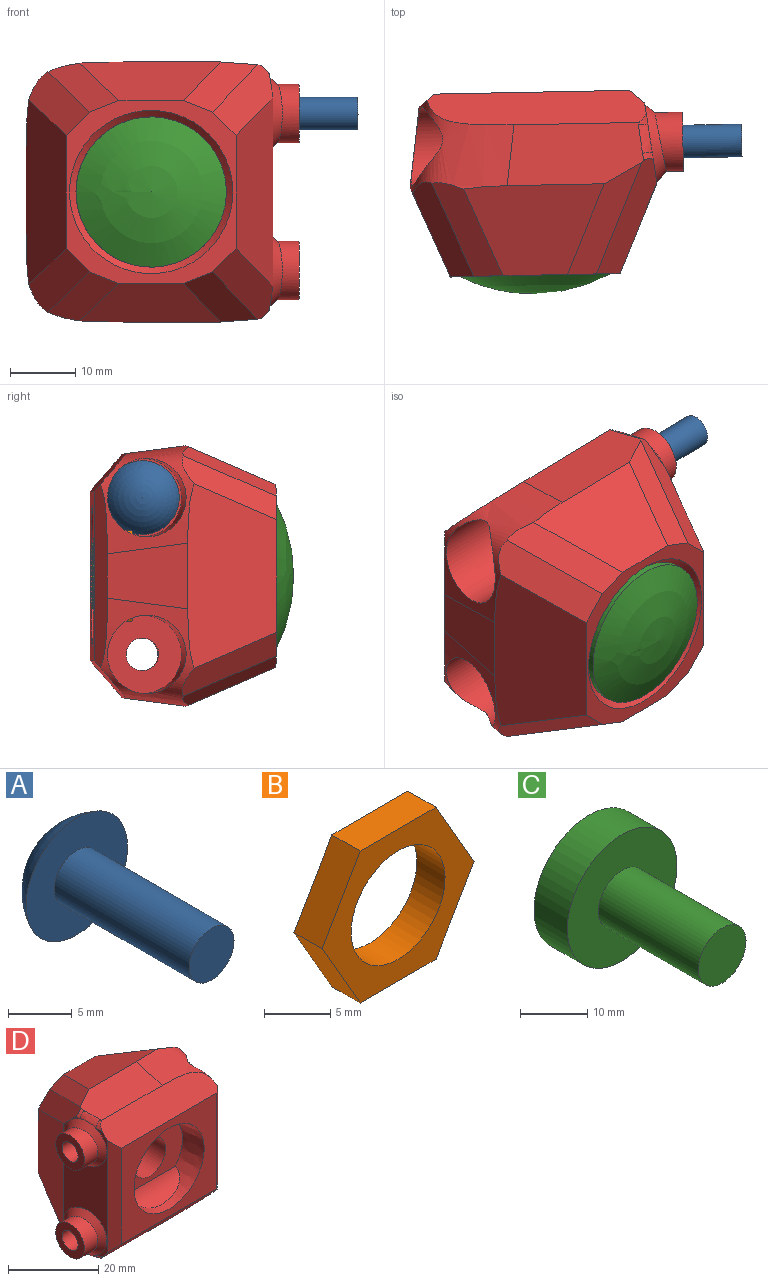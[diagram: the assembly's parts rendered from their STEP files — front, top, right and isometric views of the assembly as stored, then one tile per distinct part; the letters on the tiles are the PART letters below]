
ASSEMBLY  parts=4 mates=4
PART A: 4 faces, bbox 11.3x18.5x11.3 mm
  f0: plane 11.3x11.3mm, normal (0,-1,0), area 80.7mm2, adj f1,f3
  f1: cylinder r=2.5mm len=15mm, axis (0,-1,0), area 235.6mm2, adj f0,f2
  f2: plane 5x5mm, normal (0,-1,0), area 19.6mm2, adj f1
  f3: sphere r=6.31mm, area 138.8mm2, adj f0
PART B: 9 faces, bbox 16.2x3x14 mm
  f0: plane 7x4.04mm, normal (0.87,0,-0.5), area 24.2mm2, adj f1,f5,f7,f8
  f1: plane 7x4.04mm, normal (0.87,0,0.5), area 24.2mm2, adj f0,f2,f7,f8
  f2: plane 8.08x3mm, normal (0,0,1), area 24.2mm2, adj f1,f3,f7,f8
  f3: plane 7x4.04mm, normal (-0.87,0,0.5), area 24.2mm2, adj f2,f4,f7,f8
  f4: plane 7x4.04mm, normal (-0.87,0,-0.5), area 24.2mm2, adj f3,f5,f7,f8
  f5: plane 8.08x3mm, normal (0,0,-1), area 24.2mm2, adj f0,f4,f7,f8
  f6: cylinder r=5mm len=10mm, axis (0,1,0), area 94.2mm2, adj f7,f8
  f7: plane 16.17x14mm, normal (0,-1,0), area 91.2mm2, adj f0,f1,f2,f3,f4,f5,f6
  f8: plane 16.17x14mm, normal (0,1,0), area 91.2mm2, adj f0,f1,f2,f3,f4,f5,f6
PART C: 5 faces, bbox 23x30.8x23 mm
  f0: plane 10x10mm, normal (0,-1,0), area 78.5mm2, adj f4
  f1: sphere r=24.85mm, area 440.5mm2, adj f2
  f2: cylinder r=11.5mm len=23mm, axis (0,-1,0), area 505.8mm2, adj f1,f3
  f3: plane 23x23mm, normal (0,-1,0), area 336.9mm2, adj f2,f4
  f4: cylinder r=5mm len=21mm, axis (0,-1,0), area 659.7mm2, adj f0,f3
PART D: 48 faces, bbox 46.2x32.5x44.3 mm
  f0: cylinder r=5mm len=15mm, axis (0,-1,0), area 471.2mm2, adj f4,f15
  f1: plane 30x26mm, normal (0,-1,0), area 399.9mm2, adj f16,f26,f27,f28,f29
  f2: plane 28x26mm, normal (0,1,0), area 169.9mm2, adj f21,f22,f23,f24,f25,f30,f31,f32
  f3: cylinder r=11.5mm len=23mm, axis (0,1,0), area 433.5mm2, adj f4,f25
  f4: plane 23x23mm, normal (0,1,0), area 336.9mm2, adj f0,f3
  f5: cylinder r=2.5mm len=6mm, axis (1,0,0), area 94.2mm2, adj f6,f14
  f6: plane 12x12mm, normal (1,0,0), area 93.5mm2, adj f5,f7
  f7: cylinder r=6mm len=33.8mm, axis (1,0,0), area 1145.8mm2, adj f6,f15,f16,f47
  f8: cylinder r=2.5mm len=6mm, axis (1,0,0), area 94.2mm2, adj f9,f12
  f9: plane 12x12mm, normal (1,0,0), area 93.5mm2, adj f8,f10
  f10: cylinder r=6mm len=35.06mm, axis (1,0,0), area 1222.3mm2, adj f9,f15,f16,f46
  f11: cylinder r=4.5mm len=9mm, axis (1,0,0), area 108.4mm2, adj f12,f39
  f12: plane 9x9mm, normal (-1,0,0), area 44mm2, adj f8,f11
  f13: cylinder r=4.5mm len=9mm, axis (1,0,0), area 96.4mm2, adj f14,f38
  f14: plane 9x9mm, normal (-1,0,0), area 44mm2, adj f5,f13
  f15: plane 20.4x12.69mm, normal (0,-1,0), area 162.4mm2, adj f0,f7,f10,f16
  f16: cone r=9mm half-angle=7.6deg, axis (0,-1,0), area 286.3mm2, adj f1,f7,f10,f15
  f17: plane 21.17x9.47mm, normal (0,-0.13,-0.99), area 178.3mm2, adj f23,f28,f30,f34,f43,f44,f45,f47
  f18: plane 12.26x10.06mm, normal (0.99,-0.13,0), area 104.2mm2, adj f24,f27,f46,f47
  f19: plane 35.91x12.27mm, normal (-0.99,-0.13,0), area 194.7mm2, adj f21,f26,f28,f29,f30,f32,f38,f39
  f20: plane 21.17x9.47mm, normal (0,-0.13,0.99), area 178.2mm2, adj f22,f29,f32,f36,f40,f41,f42,f46
  f21: plane 29.05x13.76mm, normal (-0.92,0.39,0), area 346.6mm2, adj f2,f19,f30,f32
  f22: plane 22x14.26mm, normal (0,0.39,0.92), area 235.3mm2, adj f2,f20,f36,f37,f46
  f23: plane 22x14.26mm, normal (0,0.39,-0.92), area 235.3mm2, adj f2,f17,f34,f35,f47
  f24: plane 30.68x16.23mm, normal (0.92,0.39,0), area 341.1mm2, adj f2,f18,f31,f33,f46,f47
  f25: cone r=11.5mm half-angle=45deg, axis (0,1,0), area 106.6mm2, adj f2,f3
  f26: plane 30.53x2.26mm, normal (-0.66,-0.75,0), area 85.1mm2, adj f1,f19,f28,f29
  f27: plane 32.1x6.26mm, normal (0.66,-0.75,0), area 75.3mm2, adj f1,f18,f28,f29,f46,f47
  f28: plane 33.54x5.66mm, normal (0,-0.75,-0.66), area 234.6mm2, adj f1,f17,f19,f26,f27,f43,f47
  f29: plane 33.54x5.66mm, normal (0,-0.75,0.66), area 234.6mm2, adj f1,f19,f20,f26,f27,f40,f46
  f30: plane 18.01x11.38mm, normal (-0.6,0.52,-0.6), area 97.7mm2, adj f2,f17,f19,f21,f34,f45
  f31: plane 16.13x11.29mm, normal (0.6,0.52,-0.6), area 84mm2, adj f2,f24,f35,f47
  f32: plane 18.01x11.38mm, normal (-0.6,0.52,0.6), area 97.7mm2, adj f2,f19,f20,f21,f36,f42
  f33: plane 16.13x11.28mm, normal (0.6,0.52,0.6), area 84mm2, adj f2,f24,f37,f46
  f34: plane 16.91x11.7mm, normal (-0.32,0.49,-0.81), area 84.1mm2, adj f2,f17,f23,f30
  f35: plane 15.76x11.88mm, normal (0.32,0.49,-0.81), area 77.4mm2, adj f2,f23,f31,f47
  f36: plane 16.91x11.7mm, normal (-0.32,0.49,0.81), area 84.1mm2, adj f2,f20,f22,f32
  f37: plane 15.75x11.87mm, normal (0.32,0.49,0.81), area 77.4mm2, adj f2,f22,f33,f46
  f38: bspline ~11.96x11.96mm, area 69.5mm2, adj f13,f19,f44
  f39: bspline ~11.96x11.96mm, area 69.5mm2, adj f11,f19,f41
  f40: bspline ~1.81x1.72mm, area 2mm2, adj f19,f20,f29,f41
  f41: bspline ~4.45x2.08mm, area 8.7mm2, adj f20,f39,f40,f42
  f42: bspline ~1.64x1.64mm, area 2.5mm2, adj f19,f20,f32,f41
  f43: bspline ~1.81x1.72mm, area 2mm2, adj f17,f19,f28,f44
  f44: bspline ~4.6x2.08mm, area 8.7mm2, adj f17,f38,f43,f45
  f45: bspline ~8.22x2.56mm, area 2.5mm2, adj f17,f19,f30,f44
  f46: bspline ~16.86x16.86mm, area 191.3mm2, adj f10,f18,f20,f22,f24,f27,f29,f33
  f47: bspline ~16.86x16.86mm, area 187.9mm2, adj f7,f17,f18,f23,f24,f27,f28,f31
PLACE A rot(axis=(0.71,-0.7,0),180deg) t=(42.28,-7.86,25.58)mm
PLACE B rot(axis=(0,0,-1),178.9deg) t=(10.24,-6.49,13.58)mm
PLACE C rot(axis=(-0.71,-0.01,-0.71),179.2deg) t=(10.73,-31.3,13.58)mm
PLACE D rot(axis=(0,0,-1),178.9deg) t=(10.4,-14.48,-6.42)mm fixed
MATE slider B.f6 <-> C.f2  axis (0.02,-1,0) through (10.24,-6.49,13.58)mm
MATE fastened C.f2 <-> D.f3  axis (-0.02,1,0) through (10.54,-21.48,13.58)mm
MATE fastened D.f8 <-> A.f1  axis (-1,-0.02,0) through (27.28,-8.15,25.58)mm
MATE planar D.f16 <-> B.f8  axis (-0.02,1,0) through (10.24,-6.49,13.58)mm
